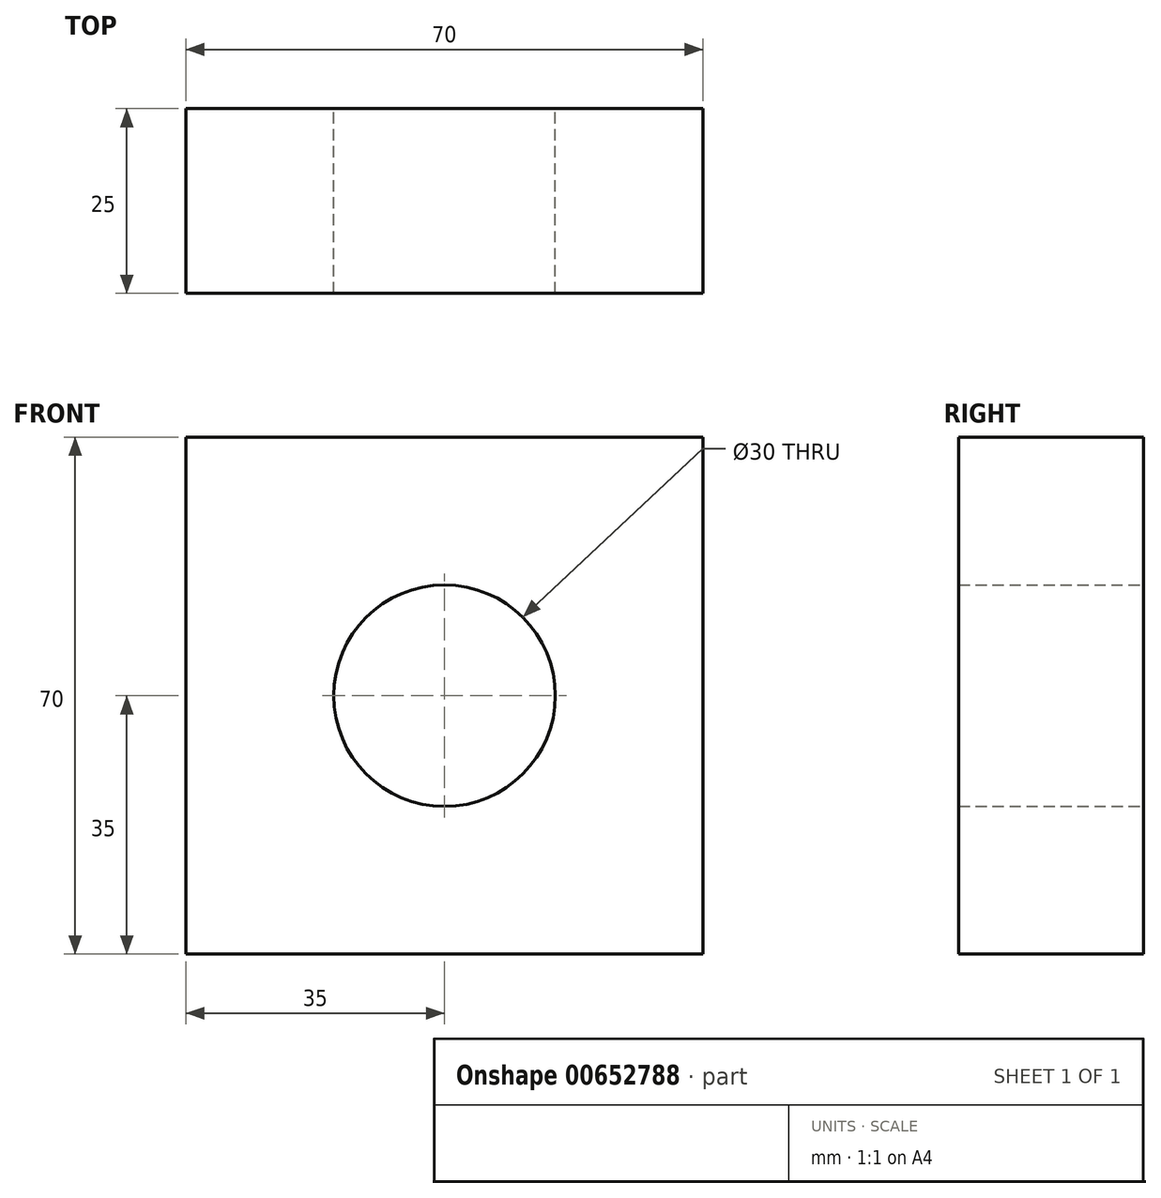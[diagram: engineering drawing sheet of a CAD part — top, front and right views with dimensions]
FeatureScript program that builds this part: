
annotation { "Feature Type Name" : "Feature", "Feature Type Description" : "" }
export const myFeature = defineFeature(function(context is Context, id is Id, definition is map)
    precondition{}
    {
        {
            var Q0;
            Q0=qCreatedBy(makeId("Front.planeOp"),FACE);
            var sketch = newSketch(context, id + "F0", { "sketchPlane" : qUnion([Q0])});
            skLineSegment(sketch, "E0.bottom", {"start": v(35, -35) * mm, "end": v(-35, -35) * mm});
            skLineSegment(sketch, "E0.top", {"start": v(35, 35) * mm, "end": v(-35, 35) * mm});
            skLineSegment(sketch, "E0.left", {"start": v(35, -35) * mm, "end": v(35, 35) * mm});
            skLineSegment(sketch, "E0.right", {"start": v(-35, -35) * mm, "end": v(-35, 35) * mm});
            skPoint(sketch, "E0.middle", {"position": v(0, 0) * mm});
            skSolve(sketch);
        }
        {
            var Q0;
            Q0=makeQuery(id+"F0.imprint","IMPRINT",FACE,{"disambiguationData":[TD([[makeQuery(id+"F0.imprint","IMPRINT",EDGE,{"derivedFrom":sQuery(id+"F0.wireOp",EDGE,"E0.bottom")}),-1.0]])]});
            extrude(context, id + "F1", {"entities" : qUnion([Q0]), "depth" : 25 * mm, "offsetDistance" : 25 * mm});
        }
        {
            var Q0;
            Q0=qCreatedBy(makeId("Front.planeOp"),FACE);
            var sketch = newSketch(context, id + "F2", { "sketchPlane" : qUnion([Q0])});
            skCircle(sketch, "E1", {"center": v(0, 0) * mm, "radius": 15 * mm});
            skSolve(sketch);
        }
        {
            var Q0;
            Q0=makeQuery(id+"F2.imprint","IMPRINT",FACE,{"disambiguationData":[TD([[makeQuery(id+"F2.imprint","IMPRINT",EDGE,{"derivedFrom":sQuery(id+"F2.wireOp",EDGE,"E1")}),1.0]])]});
            extrude(context, id + "F3", {"entities" : qUnion([Q0]), "operationType" : NewBodyOperationType.REMOVE, "depth" : 25 * mm, "offsetDistance" : 25 * mm});
        }
    });
